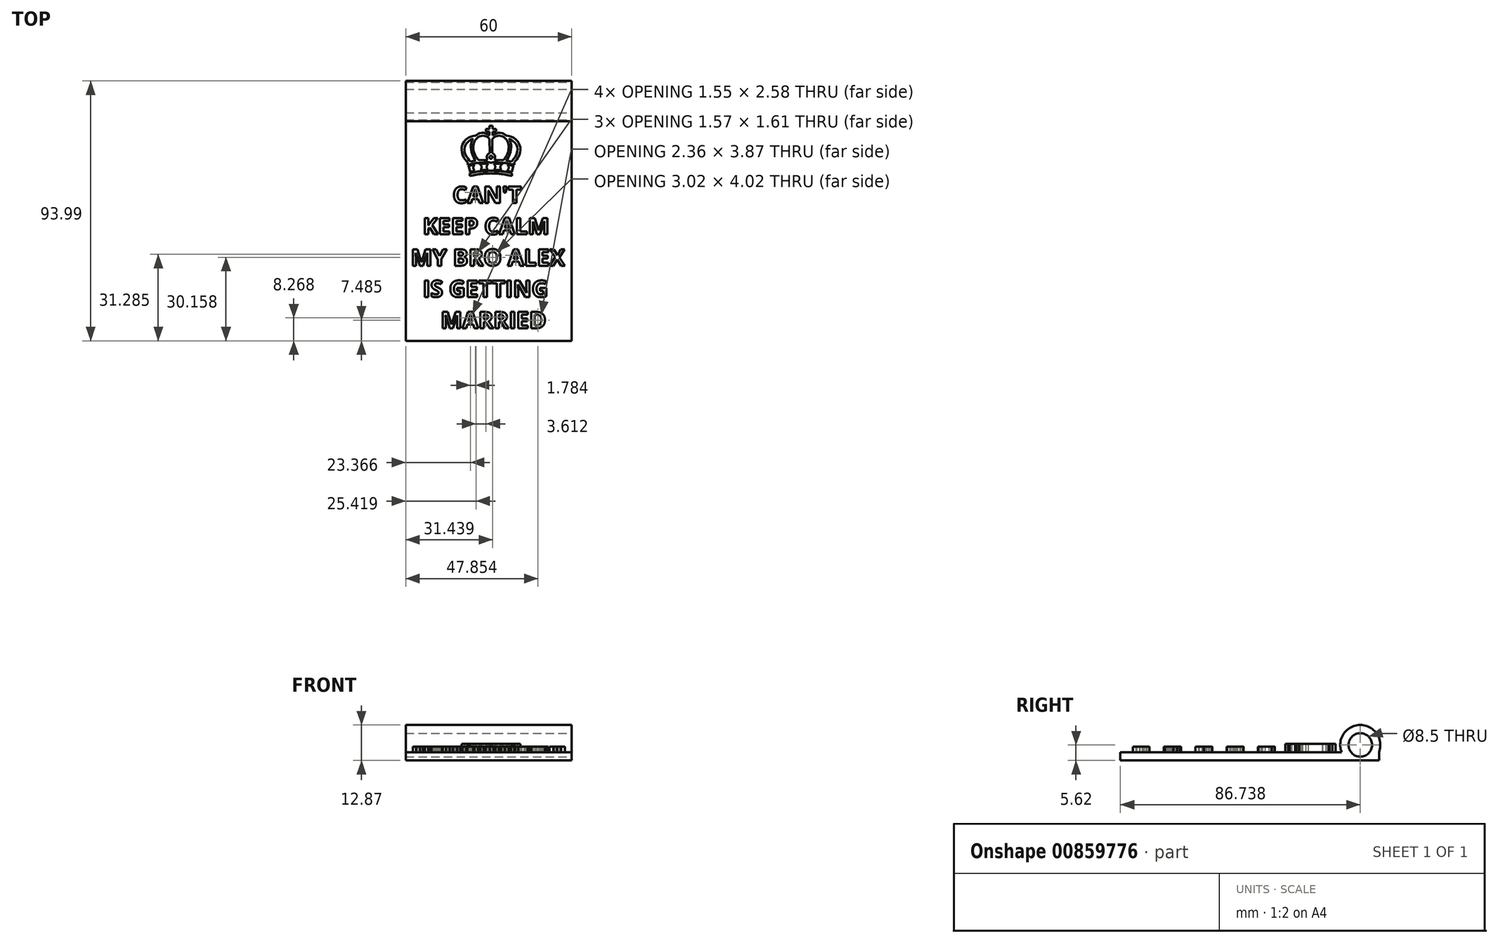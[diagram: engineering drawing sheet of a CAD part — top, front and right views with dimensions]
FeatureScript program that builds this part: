
annotation { "Feature Type Name" : "Feature", "Feature Type Description" : "" }
export const myFeature = defineFeature(function(context is Context, id is Id, definition is map)
    precondition{}
    {
        {
            var Q0;
            Q0=qCreatedBy(makeId("Top.planeOp"),FACE);
            var sketch = newSketch(context, id + "F0", { "sketchPlane" : qUnion([Q0])});
            skText(sketch, "E0", { "text": "       CAN\'T \n  KEEP CALM\nMY BRO ALEX\n  IS GETTING\n     MARRIED", "fontName": "OpenSans-Bold.ttf"});
            const initialGuessF0  = {"E0": [0.0034, -0.00369, 1, 0, 0.006]};
            skSetInitialGuess(sketch, initialGuessF0);
            skSolve(sketch);
        }
        {
            var Q0;
            Q0=qCreatedBy(makeId("Top.planeOp"),FACE);
            var sketch = newSketch(context, id + "F1", { "sketchPlane" : qUnion([Q0])});
            skLineSegment(sketch, "E1.bottom", {"start": v(1.6, 26.47) * mm, "end": v(61.6, 26.47) * mm});
            skLineSegment(sketch, "E1.top", {"start": v(1.6, -53.53) * mm, "end": v(61.6, -53.53) * mm});
            skLineSegment(sketch, "E1.left", {"start": v(1.6, 26.47) * mm, "end": v(1.6, -53.53) * mm});
            skLineSegment(sketch, "E1.right", {"start": v(61.6, 26.47) * mm, "end": v(61.6, -53.53) * mm});
            skSolve(sketch);
        }
        {
            var Q0;
            Q0 = qSketchRegion(id + "F0", true);
            extrude(context, id + "F2", {"entities" : qUnion([Q0]), "depth" : 2 * mm, "offsetDistance" : 25 * mm});
        }
        {
            var Q0;
            Q0=makeQuery(id+"F1.imprint","IMPRINT",FACE,{"disambiguationData":[TD([[makeQuery(id+"F1.imprint","IMPRINT",EDGE,{"derivedFrom":sQuery(id+"F1.wireOp",EDGE,"E1.bottom")}),-1.0]])]});
            extrude(context, id + "F3", {"entities" : qUnion([Q0]), "oppositeDirection" : true, "depth" : 3 * mm, "offsetDistance" : 25 * mm});
        }
        {
            var Q0;
            Q0=qCreatedBy(makeId("Top.planeOp"),FACE);
            var sketch = newSketch(context, id + "F4", { "sketchPlane" : qUnion([Q0])});
            skLineSegment(sketch, "E2", {"start": v(40.06, 6.12) * mm, "end": v(40.06, 7.14) * mm});
            skLineSegment(sketch, "E3", {"start": v(33.35, 10.6) * mm, "end": v(36.57, 10.42) * mm});
            skFitSpline(sketch, "E4", {"points": [v(36.57, 10.42) * mm, v(36.07, 10) * mm, v(35.85, 9.27) * mm, v(36.07, 8.27) * mm], "startDerivative": vector(-1.85, -1.2) * mm, "endDerivative": vector(0.86, -2.71) * mm});
            skLineSegment(sketch, "E5", {"start": v(36.07, 8.27) * mm, "end": v(33.7, 8.38) * mm});
            skFitSpline(sketch, "E6", {"points": [v(33.7, 8.38) * mm, v(33.88, 8.87) * mm, v(34, 9.5) * mm, v(33.7, 10.16) * mm, v(33.35, 10.6) * mm], "startDerivative": vector(0.72, 2.03) * mm, "endDerivative": vector(-1.5, 1.67) * mm});
            skLineSegment(sketch, "E7", {"start": v(38.27, 7.98) * mm, "end": v(40.03, 7.6) * mm});
            skLineSegment(sketch, "E8", {"start": v(40.03, 7.6) * mm, "end": v(40.48, 9.73) * mm});
            skLineSegment(sketch, "E9", {"start": v(40.48, 9.73) * mm, "end": v(38.39, 10.17) * mm});
            skFitSpline(sketch, "E10", {"points": [v(38.39, 10.17) * mm, v(38.8, 9.36) * mm, v(38.69, 8.54) * mm, v(38.27, 7.98) * mm], "startDerivative": vector(1.5, -2.21) * mm, "endDerivative": vector(-1.5, -1.65) * mm});
            skLineSegment(sketch, "E11", {"start": v(40.9, 10.1) * mm, "end": v(40.9, 11.1) * mm});
            skFitSpline(sketch, "E12", {"points": [v(40.9, 11.1) * mm, v(41.8, 12.1) * mm, v(42.96, 14.57) * mm, v(42.62, 17.77) * mm, v(40.06, 20.27) * mm, v(38, 20.72) * mm, v(37.07, 21.39) * mm, v(35.62, 21.72) * mm, v(33.86, 21.31) * mm, v(32.97, 20.75) * mm, v(32.97, 20.83) * mm], "startDerivative": vector(9.67, 9.7) * mm, "endDerivative": vector(1.15, 4.78) * mm});
            skLineSegment(sketch, "E13", {"start": v(32.97, 20.83) * mm, "end": v(32.97, 22.06) * mm});
            skLineSegment(sketch, "E14", {"start": v(32.97, 22.06) * mm, "end": v(34.22, 22.06) * mm});
            skLineSegment(sketch, "E15", {"start": v(34.22, 22.06) * mm, "end": v(34.22, 23.06) * mm});
            skLineSegment(sketch, "E16", {"start": v(34.22, 23.06) * mm, "end": v(32.97, 23.06) * mm});
            skLineSegment(sketch, "E17", {"start": v(32.97, 23.06) * mm, "end": v(32.97, 24.26) * mm});
            skLineSegment(sketch, "E18", {"start": v(32.97, 24.26) * mm, "end": v(32.44, 24.26) * mm});
            skLineSegment(sketch, "E19", {"start": v(32.44, 25) * mm, "end": v(32.44, 4.45) * mm, "construction": true});
            skFitSpline(sketch, "E20", {"points": [v(32.95, 19.47) * mm, v(33.86, 20.27) * mm, v(35.5, 20.7) * mm, v(37.2, 20.08) * mm, v(38.36, 18.7) * mm, v(38.8, 16.98) * mm, v(38.64, 14.8) * mm, v(37.8, 13.05) * mm, v(36.82, 11.82) * mm], "startDerivative": vector(7.67, 8.23) * mm, "endDerivative": vector(-8.49, -9.77) * mm});
            skLineSegment(sketch, "E21", {"start": v(36.82, 11.82) * mm, "end": v(33.63, 11.93) * mm});
            skLineSegment(sketch, "E22", {"start": v(32.91, 14.33) * mm, "end": v(32.95, 19.47) * mm});
            skLineSegment(sketch, "E23", {"start": v(37.9, 11.7) * mm, "end": v(39.83, 11.35) * mm});
            skFitSpline(sketch, "E24", {"points": [v(39.83, 11.35) * mm, v(40.79, 12.37) * mm, v(41.86, 14.48) * mm, v(41.95, 16.68) * mm, v(40.94, 18.28) * mm, v(39.1, 19.53) * mm, v(39.15, 19.32) * mm, v(39.57, 18.32) * mm, v(39.71, 16.91) * mm, v(39.59, 15.3) * mm, v(38.64, 12.68) * mm, v(37.9, 11.7) * mm], "startDerivative": vector(11.11, 10.41) * mm, "endDerivative": vector(-9.14, -9.9) * mm});
            skFitSpline(sketch, "E25", {"points": [v(40.9, 10.1) * mm, v(38.3, 10.65) * mm, v(35.16, 11) * mm, v(32.44, 10.97) * mm], "startDerivative": vector(-7.82, 1.8) * mm, "endDerivative": vector(-8.14, -0.28) * mm});
            skFitSpline(sketch, "E26", {"points": [v(40.06, 6.12) * mm, v(38.07, 6.5) * mm, v(35.72, 6.88) * mm, v(32.44, 7.06) * mm], "startDerivative": vector(-6.62, 1.3) * mm, "endDerivative": vector(-9, 0.27) * mm});
            skFitSpline(sketch, "E27", {"points": [v(40.06, 7.14) * mm, v(38.42, 7.5) * mm, v(36.04, 7.83) * mm, v(33.73, 7.94) * mm, v(32.44, 7.96) * mm], "startDerivative": vector(-6.65, 1.58) * mm, "endDerivative": vector(-5.8, 0.06) * mm});
            skArc(sketch, "E28", {"start": v(32.44, 12.33) * mm, "mid": v(32.98, 12.88) * mm, "end": v(32.44, 13.43) * mm});
            skArc(sketch, "E29", {"start": v(33.63, 11.93) * mm, "mid": v(33.9, 13.32) * mm, "end": v(32.91, 14.33) * mm});
            skLineSegment(sketch, "E30.MirrorCS", {"start": v(31.9, 24.26) * mm, "end": v(32.44, 24.26) * mm});
            skLineSegment(sketch, "E31.MirrorCS", {"start": v(31.9, 20.83) * mm, "end": v(31.9, 22.06) * mm});
            skLineSegment(sketch, "E32.MirrorCS", {"start": v(28.05, 11.82) * mm, "end": v(31.24, 11.93) * mm});
            skArc(sketch, "E33.MirrorCS", {"start": v(31.24, 11.93) * mm, "mid": v(30.97, 13.32) * mm, "end": v(31.96, 14.33) * mm});
            skLineSegment(sketch, "E34.MirrorCS", {"start": v(26.6, 7.98) * mm, "end": v(24.84, 7.6) * mm});
            skFitSpline(sketch, "E35.MirrorCS", {"points": [v(24.8, 7.14) * mm, v(26.45, 7.5) * mm, v(28.83, 7.83) * mm, v(31.14, 7.94) * mm, v(32.44, 7.96) * mm], "startDerivative": vector(6.65, 1.58) * mm, "endDerivative": vector(5.8, 0.06) * mm});
            skLineSegment(sketch, "E36.MirrorCS", {"start": v(24.8, 6.12) * mm, "end": v(24.8, 7.14) * mm});
            skLineSegment(sketch, "E37.MirrorCS", {"start": v(28.8, 8.27) * mm, "end": v(31.16, 8.38) * mm});
            skFitSpline(sketch, "E38.MirrorCS", {"points": [v(25.04, 11.35) * mm, v(24.08, 12.37) * mm, v(23.01, 14.48) * mm, v(22.92, 16.68) * mm, v(23.93, 18.28) * mm, v(25.78, 19.53) * mm, v(25.72, 19.32) * mm, v(25.3, 18.32) * mm, v(25.16, 16.91) * mm, v(25.28, 15.3) * mm, v(26.23, 12.68) * mm, v(26.97, 11.7) * mm], "startDerivative": vector(-11.11, 10.41) * mm, "endDerivative": vector(9.14, -9.9) * mm});
            skLineSegment(sketch, "E39.MirrorCS", {"start": v(24.84, 7.6) * mm, "end": v(24.39, 9.73) * mm});
            skFitSpline(sketch, "E40.MirrorCS", {"points": [v(28.3, 10.42) * mm, v(28.8, 10) * mm, v(29.02, 9.27) * mm, v(28.8, 8.27) * mm], "startDerivative": vector(1.85, -1.2) * mm, "endDerivative": vector(-0.86, -2.71) * mm});
            skLineSegment(sketch, "E41.MirrorCS", {"start": v(31.9, 23.06) * mm, "end": v(31.9, 24.26) * mm});
            skLineSegment(sketch, "E42.MirrorCS", {"start": v(30.65, 22.06) * mm, "end": v(30.65, 23.06) * mm});
            skArc(sketch, "E43.MirrorCS", {"start": v(32.44, 12.33) * mm, "mid": v(31.89, 12.88) * mm, "end": v(32.44, 13.43) * mm});
            skLineSegment(sketch, "E44.MirrorCS", {"start": v(23.96, 10.1) * mm, "end": v(23.96, 11.1) * mm});
            skFitSpline(sketch, "E45.MirrorCS", {"points": [v(31.92, 19.47) * mm, v(31, 20.27) * mm, v(29.37, 20.7) * mm, v(27.68, 20.08) * mm, v(26.5, 18.7) * mm, v(26.08, 16.98) * mm, v(26.23, 14.8) * mm, v(27.06, 13.05) * mm, v(28.05, 11.82) * mm], "startDerivative": vector(-7.67, 8.23) * mm, "endDerivative": vector(8.49, -9.77) * mm});
            skLineSegment(sketch, "E46.MirrorCS", {"start": v(31.96, 14.33) * mm, "end": v(31.92, 19.47) * mm});
            skLineSegment(sketch, "E47.MirrorCS", {"start": v(31.52, 10.6) * mm, "end": v(28.3, 10.42) * mm});
            skFitSpline(sketch, "E48.MirrorCS", {"points": [v(31.16, 8.38) * mm, v(31, 8.87) * mm, v(30.87, 9.5) * mm, v(31.16, 10.16) * mm, v(31.52, 10.6) * mm], "startDerivative": vector(-0.72, 2.03) * mm, "endDerivative": vector(1.5, 1.67) * mm});
            skLineSegment(sketch, "E49.MirrorCS", {"start": v(26.97, 11.7) * mm, "end": v(25.04, 11.35) * mm});
            skLineSegment(sketch, "E50.MirrorCS", {"start": v(30.65, 23.06) * mm, "end": v(31.9, 23.06) * mm});
            skFitSpline(sketch, "E51.MirrorCS", {"points": [v(26.48, 10.17) * mm, v(26.07, 9.36) * mm, v(26.18, 8.54) * mm, v(26.6, 7.98) * mm], "startDerivative": vector(-1.5, -2.21) * mm, "endDerivative": vector(1.5, -1.65) * mm});
            skFitSpline(sketch, "E52.MirrorCS", {"points": [v(23.96, 10.1) * mm, v(26.57, 10.65) * mm, v(29.71, 11) * mm, v(32.44, 10.97) * mm], "startDerivative": vector(7.82, 1.8) * mm, "endDerivative": vector(8.14, -0.28) * mm});
            skLineSegment(sketch, "E53.MirrorCS", {"start": v(24.39, 9.73) * mm, "end": v(26.48, 10.17) * mm});
            skFitSpline(sketch, "E54.MirrorCS", {"points": [v(23.96, 11.1) * mm, v(23.07, 12.1) * mm, v(21.91, 14.57) * mm, v(22.25, 17.77) * mm, v(24.8, 20.27) * mm, v(26.87, 20.72) * mm, v(27.8, 21.39) * mm, v(29.25, 21.72) * mm, v(31, 21.31) * mm, v(31.9, 20.75) * mm, v(31.9, 20.83) * mm], "startDerivative": vector(-9.67, 9.7) * mm, "endDerivative": vector(-1.15, 4.78) * mm});
            skFitSpline(sketch, "E55.MirrorCS", {"points": [v(24.8, 6.12) * mm, v(26.8, 6.5) * mm, v(29.15, 6.88) * mm, v(32.44, 7.06) * mm], "startDerivative": vector(6.62, 1.3) * mm, "endDerivative": vector(9, 0.27) * mm});
            skLineSegment(sketch, "E56.MirrorCS", {"start": v(31.9, 22.06) * mm, "end": v(30.65, 22.06) * mm});
            skSolve(sketch);
        }
        {
            var Q0;
            Q0 = qSketchRegion(id + "F4", true);
            extrude(context, id + "F5", {"entities" : qUnion([Q0]), "operationType" : NewBodyOperationType.ADD, "depth" : 3 * mm, "offsetDistance" : 25 * mm});
        }
        {
            var Q0;
            Q0=makeQuery(id+"F3.opExtrude","SWEPT_FACE",FACE,{"disambiguationData":[OSD([sQuery(id+"F1.wireOp",EDGE,"E1.right")])]});
            var sketch = newSketch(context, id + "F6", { "sketchPlane" : qUnion([Q0])});
            skCircle(sketch, "E57", {"center": v(33.2, 2.62) * mm, "radius": 4.25 * mm});
            skArc(sketch, "E58", {"start": v(39.97, 0) * mm, "mid": v(33.2, 9.87) * mm, "end": v(26.45, 0) * mm});
            skLineSegment(sketch, "E59.bottom", {"start": v(26.47, -3) * mm, "end": v(39.97, -3) * mm});
            skLineSegment(sketch, "E59.left", {"start": v(26.47, -3) * mm, "end": v(26.47, 0) * mm});
            skLineSegment(sketch, "E59.right", {"start": v(39.97, -3) * mm, "end": v(39.97, 0) * mm});
            skSolve(sketch);
        }
        {
            var Q0;
            Q0=makeQuery(id+"F6.imprint","IMPRINT",FACE,{"disambiguationData":[TD([[makeQuery(id+"F6.imprint","IMPRINT",EDGE,{"derivedFrom":sQuery(id+"F6.wireOp",EDGE,"E57")}),-1.0]])]});
            extrude(context, id + "F7", {"entities" : qUnion([Q0]), "operationType" : NewBodyOperationType.ADD, "oppositeDirection" : true, "depth" : 60 * mm, "offsetDistance" : 25 * mm});
        }
    });
